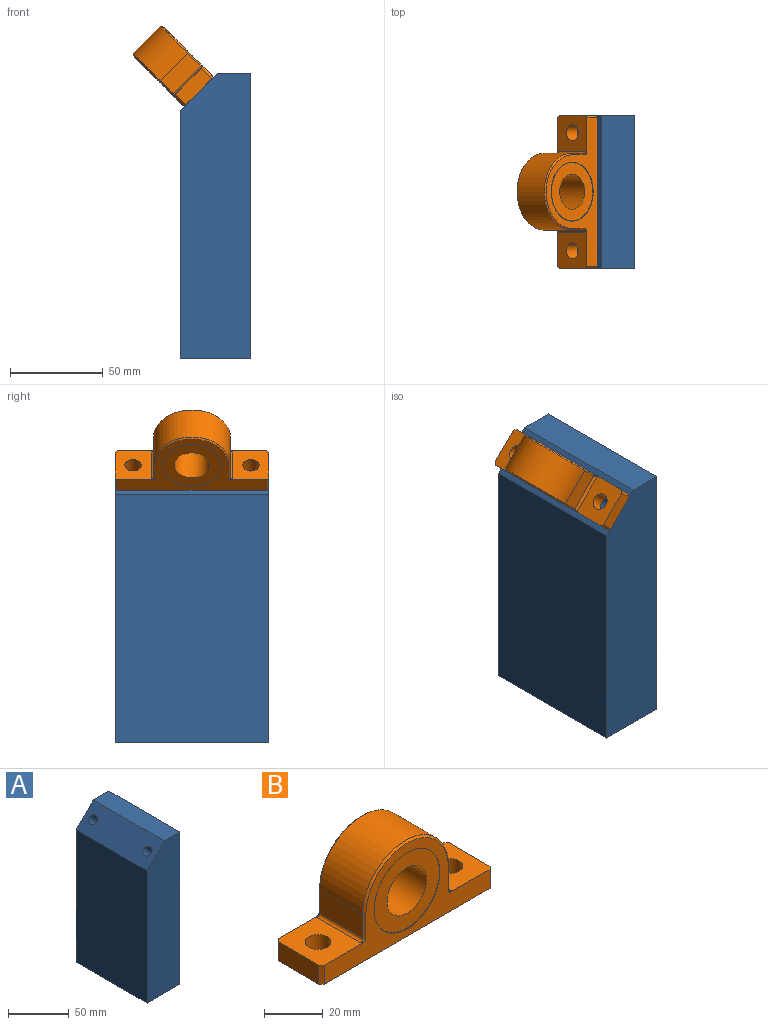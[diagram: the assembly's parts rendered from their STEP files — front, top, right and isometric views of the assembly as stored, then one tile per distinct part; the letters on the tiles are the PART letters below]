
ASSEMBLY  parts=2 mates=1
PART A: 15 faces, bbox 38.1x82.6x153.4 mm
  f0: plane 82.55x38.1mm, normal (0,0,-1), area 3025.2mm2, adj f1,f2,f5,f6,f11,f13
  f1: plane 133.35x82.55mm, normal (-1,0,0), area 11008mm2, adj f0,f4,f5,f6
  f2: plane 153.37x82.55mm, normal (1,0,0), area 12660.3mm2, adj f0,f3,f5,f6
  f3: plane 82.55x18.09mm, normal (0,0,1), area 1492.9mm2, adj f2,f4,f5,f6
  f4: plane 82.55x20.02mm, normal (-0.71,0,0.71), area 2216.9mm2, adj f1,f3,f5,f6,f7,f9
  f5: plane 153.37x38.1mm, normal (0,-1,0), area 5642.9mm2, adj f0,f1,f2,f3,f4
  f6: plane 153.37x38.1mm, normal (0,1,0), area 5642.9mm2, adj f0,f1,f2,f3,f4
  f7: cylinder r=4.36mm len=24.13mm, axis (-0.71,0,0.71), area 696.6mm2, adj f4,f8
  f8: plane 8.73x6.17mm, normal (-0.71,0,0.71), area 59.9mm2, adj f7
  f9: cylinder r=4.36mm len=24.13mm, axis (-0.71,0,0.71), area 696.6mm2, adj f4,f10
  f10: plane 8.73x6.17mm, normal (-0.71,0,0.71), area 59.9mm2, adj f9
  f11: cylinder r=4.37mm len=25.4mm, axis (0,0,-1), area 697.2mm2, adj f0,f12
  f12: plane 8.74x8.74mm, normal (0,0,-1), area 60mm2, adj f11
  f13: cylinder r=4.37mm len=25.4mm, axis (0,0,-1), area 697.2mm2, adj f0,f14
  f14: plane 8.74x8.74mm, normal (0,0,-1), area 60mm2, adj f13
PART B: 36 faces, bbox 82.6x24x39.7 mm
  f0: cylinder r=15.88mm len=31.75mm, axis (0,-1,0), area 25.3mm2, adj f10,f32
  f1: cylinder r=15.88mm len=31.75mm, axis (0,-1,0), area 2077.5mm2, adj f11,f30
  f2: cylinder r=20.64mm len=41.28mm, axis (0,1,0), area 1342.1mm2, adj f3,f9,f13,f16
  f3: plane 20.7x9.84mm, normal (-1,0,0), area 203.7mm2, adj f2,f14,f17,f19
  f4: plane 22.23x19.6mm, normal (0,0,1), area 369mm2, adj f5,f10,f11,f18,f19,f20,f24,f25
  f5: plane 19.69x7.94mm, normal (-1,0,0), area 156.2mm2, adj f4,f6,f24,f25
  f6: plane 82.55x22.23mm, normal (0,0,-1), area 1711.7mm2, adj f5,f7,f10,f11,f24,f25,f26,f27
  f7: plane 19.69x7.94mm, normal (1,0,0), area 156.2mm2, adj f6,f8,f26,f27
  f8: plane 22.23x19.6mm, normal (0,0,1), area 369mm2, adj f7,f10,f11,f21,f22,f23,f26,f27
  f9: plane 20.7x9.84mm, normal (1,0,0), area 203.7mm2, adj f2,f12,f15,f22
  f10: plane 80.01x38.93mm, normal (0,-1,0), area 906.6mm2, adj f0,f4,f6,f8,f15,f16,f17,f18
  f11: plane 80.01x38.93mm, normal (0,1,0), area 906.6mm2, adj f1,f4,f6,f8,f12,f13,f14,f20
  f12: plane 9.84x0.76mm, normal (0.71,0.71,0), area 10.6mm2, adj f9,f11,f13,f23
  f13: cone r=20.64mm half-angle=45deg, axis (0,-1,0), area 68.6mm2, adj f2,f11,f12,f14
  f14: plane 9.84x0.76mm, normal (-0.71,0.71,0), area 10.6mm2, adj f3,f11,f13,f20
  f15: plane 9.84x0.76mm, normal (0.71,-0.71,0), area 10.6mm2, adj f9,f10,f16,f21
  f16: cone r=19.88mm half-angle=45deg, axis (0,1,0), area 68.6mm2, adj f2,f10,f15,f17
  f17: plane 9.84x0.76mm, normal (-0.71,-0.71,0), area 10.6mm2, adj f3,f10,f16,f18
  f18: cylinder r=1.27mm len=2.03mm, axis (-0.71,0.71,0), area 1.6mm2, adj f4,f10,f17,f19
  f19: cylinder r=1.27mm len=21.75mm, axis (0,-1,0), area 42.1mm2, adj f3,f4,f18,f20
  f20: cylinder r=1.27mm len=2.03mm, axis (-0.71,-0.71,0), area 1.6mm2, adj f4,f11,f14,f19
  f21: cylinder r=1.27mm len=2.03mm, axis (-0.71,-0.71,0), area 1.6mm2, adj f8,f10,f15,f22
  f22: cylinder r=1.27mm len=21.75mm, axis (0,-1,0), area 42.1mm2, adj f8,f9,f21,f23
  f23: cylinder r=1.27mm len=2.03mm, axis (-0.71,0.71,0), area 1.6mm2, adj f8,f11,f12,f22
  f24: plane 7.94x1.27mm, normal (-0.71,0.71,0), area 14.3mm2, adj f4,f5,f6,f11
  f25: plane 7.94x1.27mm, normal (-0.71,-0.71,0), area 14.3mm2, adj f4,f5,f6,f10
  f26: plane 7.94x1.27mm, normal (0.71,0.71,0), area 14.3mm2, adj f6,f7,f8,f11
  f27: plane 7.94x1.27mm, normal (0.71,-0.71,0), area 14.3mm2, adj f6,f7,f8,f10
  f28: plane 31.5x31.5mm, normal (0,1,0), area 494.1mm2, adj f29,f33
  f29: cylinder r=15.75mm len=31.5mm, axis (0,-1,0), area 2060.9mm2, adj f28,f30
  f30: plane 31.75x31.75mm, normal (0,1,0), area 12.6mm2, adj f1,f29
  f31: plane 31.5x31.5mm, normal (0,-1,0), area 494.1mm2, adj f32,f33
  f32: cone r=15.88mm half-angle=45deg, axis (0,1,0), area 17.8mm2, adj f0,f31
  f33: cylinder r=9.53mm len=22.1mm, axis (0,-1,0), area 1322.5mm2, adj f28,f31
  f34: cylinder r=4.37mm len=8.73mm, axis (0,0,1), area 217.7mm2, adj f4,f6
  f35: cylinder r=4.37mm len=8.73mm, axis (0,0,1), area 217.7mm2, adj f6,f8
PLACE A t=(-39.42,59.09,-32.32)mm
PLACE B rot(axis=(-0.36,-0.36,0.86),98.4deg) t=(-42.88,17.82,124.51)mm
MATE fastened B.f34 <-> A.f7  axis (0.71,0,-0.71) through (-29.41,-13.93,111.04)mm
